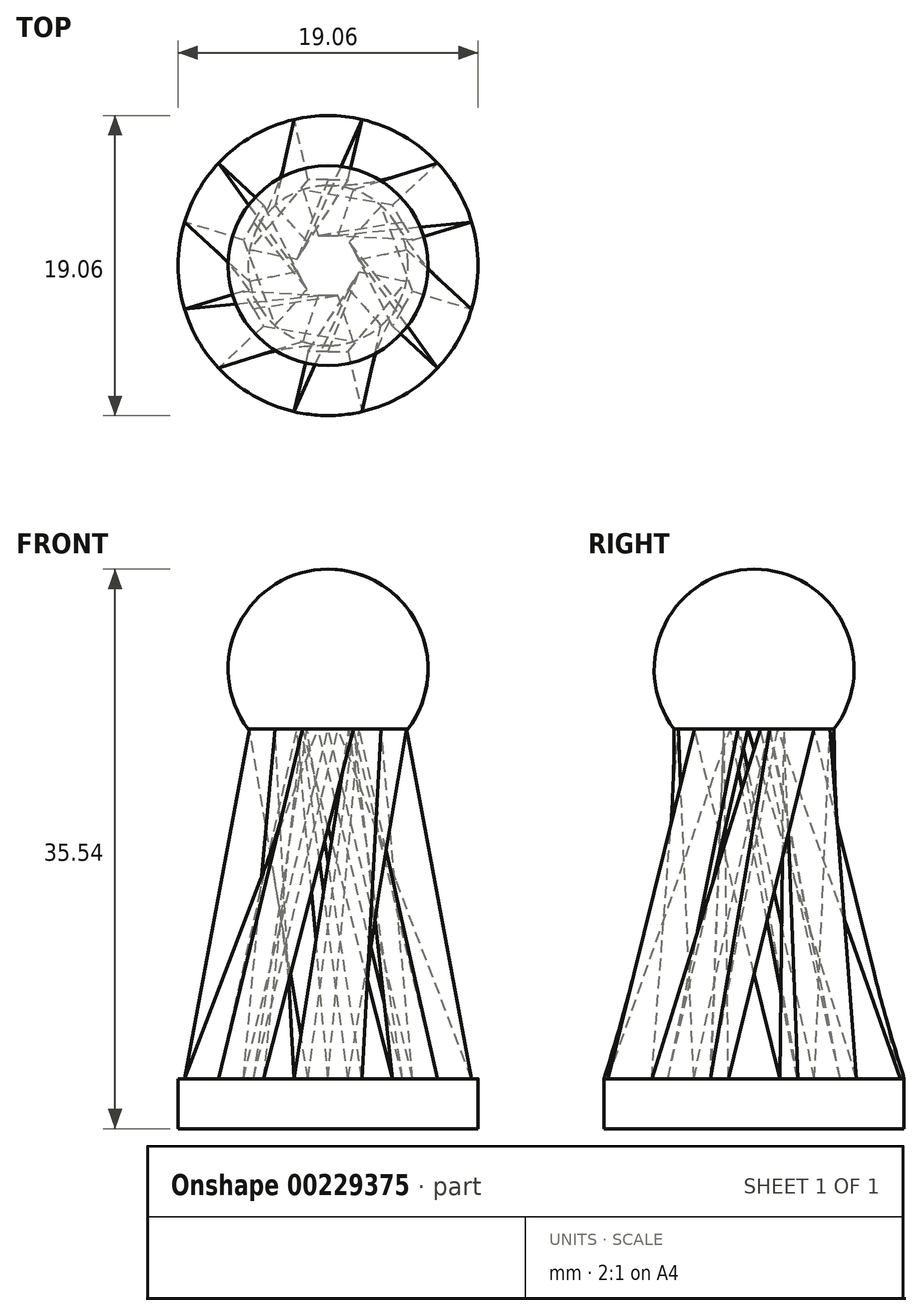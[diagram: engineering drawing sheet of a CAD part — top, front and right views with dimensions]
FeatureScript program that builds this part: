
annotation { "Feature Type Name" : "Feature", "Feature Type Description" : "" }
export const myFeature = defineFeature(function(context is Context, id is Id, definition is map)
    precondition{}
    {
        {
            var Q0;
            Q0=qCreatedBy(makeId("Top.planeOp"),FACE);
            var sketch = newSketch(context, id + "F0", { "sketchPlane" : qUnion([Q0])});
            skCircle(sketch, "E0", {"center": v(0, 0) * mm, "radius": 9.53 * mm});
            skSolve(sketch);
        }
        {
            var Q0;
            Q0=makeQuery(id+"F0.imprint","IMPRINT",FACE,{"disambiguationData":[TD([[makeQuery(id+"F0.imprint","IMPRINT",EDGE,{"derivedFrom":sQuery(id+"F0.wireOp",EDGE,"E0")}),1.0]])]});
            extrude(context, id + "F1", {"entities" : qUnion([Q0]), "depth" : 3.17 * mm});
        }
        {
            var Q0;
            Q0=makeQuery(id+"F1.opExtrude","CAP_FACE",FACE,{"disambiguationData":[OSD([sQuery(id+"F0.wireOp",EDGE,"E0")])],"isStart":false});
            var sketch = newSketch(context, id + "F2", { "sketchPlane" : qUnion([Q0])});
            skLineSegment(sketch, "E1", {"start": v(0, -5.47) * mm, "end": v(-1.27, -5.47) * mm});
            skLineSegment(sketch, "E2", {"start": v(0, -5.47) * mm, "end": v(1.27, -5.47) * mm});
            skLineSegment(sketch, "E3", {"start": v(-1.27, -5.47) * mm, "end": v(-2.15, -9.28) * mm});
            skLineSegment(sketch, "E4", {"start": v(1.27, -5.47) * mm, "end": v(2.15, -9.28) * mm});
            skLineSegment(sketch, "E5.1.0", {"start": v(-4.74, -2.73) * mm, "end": v(-5.37, -1.63) * mm});
            skLineSegment(sketch, "E5.1.1", {"start": v(-4.74, -2.73) * mm, "end": v(-4.1, -3.83) * mm});
            skLineSegment(sketch, "E5.1.2", {"start": v(-4.1, -3.83) * mm, "end": v(-6.96, -6.5) * mm});
            skLineSegment(sketch, "E5.1.3", {"start": v(-5.37, -1.63) * mm, "end": v(-9.11, -2.77) * mm});
            skLineSegment(sketch, "E5.2.0", {"start": v(-4.74, 2.73) * mm, "end": v(-4.1, 3.83) * mm});
            skLineSegment(sketch, "E5.2.1", {"start": v(-4.74, 2.73) * mm, "end": v(-5.37, 1.63) * mm});
            skLineSegment(sketch, "E5.2.2", {"start": v(-5.37, 1.63) * mm, "end": v(-9.11, 2.77) * mm});
            skLineSegment(sketch, "E5.2.3", {"start": v(-4.1, 3.83) * mm, "end": v(-6.96, 6.5) * mm});
            skLineSegment(sketch, "E5.3.0", {"start": v(0, 5.47) * mm, "end": v(1.27, 5.47) * mm});
            skLineSegment(sketch, "E5.3.1", {"start": v(0, 5.47) * mm, "end": v(-1.27, 5.47) * mm});
            skLineSegment(sketch, "E5.3.2", {"start": v(-1.27, 5.47) * mm, "end": v(-2.15, 9.28) * mm});
            skLineSegment(sketch, "E5.3.3", {"start": v(1.27, 5.47) * mm, "end": v(2.15, 9.28) * mm});
            skLineSegment(sketch, "E5.4.0", {"start": v(4.74, 2.73) * mm, "end": v(5.37, 1.63) * mm});
            skLineSegment(sketch, "E5.4.1", {"start": v(4.74, 2.73) * mm, "end": v(4.1, 3.83) * mm});
            skLineSegment(sketch, "E5.4.2", {"start": v(4.1, 3.83) * mm, "end": v(6.96, 6.5) * mm});
            skLineSegment(sketch, "E5.4.3", {"start": v(5.37, 1.63) * mm, "end": v(9.11, 2.77) * mm});
            skLineSegment(sketch, "E5.5.0", {"start": v(4.74, -2.73) * mm, "end": v(4.1, -3.83) * mm});
            skLineSegment(sketch, "E5.5.1", {"start": v(4.74, -2.73) * mm, "end": v(5.37, -1.63) * mm});
            skLineSegment(sketch, "E5.5.2", {"start": v(5.37, -1.63) * mm, "end": v(9.11, -2.77) * mm});
            skLineSegment(sketch, "E5.5.3", {"start": v(4.1, -3.83) * mm, "end": v(6.96, -6.5) * mm});
            skPoint(sketch, "E5.center", {"position": v(0, 0) * mm});
            skLineSegment(sketch, "E5.anchor1", {"start": v(0, 0) * mm, "end": v(-1.27, -5.47) * mm, "construction": true});
            skLineSegment(sketch, "E5.anchor2", {"start": v(0, 0) * mm, "end": v(4.1, -3.83) * mm, "construction": true});
            skArc(sketch, "E6", {"start": v(-2.15, -9.28) * mm, "mid": v(0, -9.52) * mm, "end": v(2.15, -9.28) * mm});
            skArc(sketch, "E7.trimOffspring", {"start": v(-9.11, -2.77) * mm, "mid": v(-8.25, -4.76) * mm, "end": v(-6.96, -6.5) * mm});
            skArc(sketch, "E8.trimOffspring", {"start": v(-6.96, 6.5) * mm, "mid": v(-8.25, 4.76) * mm, "end": v(-9.11, 2.77) * mm});
            skArc(sketch, "E9.trimOffspring", {"start": v(2.15, 9.28) * mm, "mid": v(0, 9.52) * mm, "end": v(-2.15, 9.28) * mm});
            skArc(sketch, "E10.trimOffspring", {"start": v(9.11, 2.77) * mm, "mid": v(8.25, 4.76) * mm, "end": v(6.96, 6.5) * mm});
            skArc(sketch, "E11.trimOffspring", {"start": v(6.96, -6.5) * mm, "mid": v(8.25, -4.76) * mm, "end": v(9.11, -2.77) * mm});
            skLineSegment(sketch, "E12", {"start": v(0, -5.47) * mm, "end": v(0, 0) * mm});
            skSolve(sketch);
        }
        {
            var Q0;
            Q0=qCreatedBy(makeId("Top.planeOp"),FACE);
            cPlane(context, id + "F3", {"entities" : qUnion([Q0]), "cplaneType" : CPlaneType.OFFSET, "offset" : 25.4 * mm, "width" : 152.4 * mm, "height" : 152.4 * mm});
        }
        {
            var Q0;
            Q0=qCreatedBy(id+"F3.planeOp",FACE);
            var sketch = newSketch(context, id + "F4", { "sketchPlane" : qUnion([Q0])});
            skArc(sketch, "E13", {"start": v(-1.6, -4.82) * mm, "mid": v(0, -5.08) * mm, "end": v(1.6, -4.82) * mm});
            skLineSegment(sketch, "E14", {"start": v(0, -1.9) * mm, "end": v(0.64, -1.9) * mm});
            skLineSegment(sketch, "E15", {"start": v(0, -1.9) * mm, "end": v(-0.64, -1.9) * mm});
            skLineSegment(sketch, "E16", {"start": v(-0.63, -1.9) * mm, "end": v(-1.6, -4.82) * mm});
            skLineSegment(sketch, "E17", {"start": v(0.63, -1.9) * mm, "end": v(1.6, -4.82) * mm});
            skLineSegment(sketch, "E18.1.0", {"start": v(1.33, -1.5) * mm, "end": v(3.37, -3.8) * mm});
            skLineSegment(sketch, "E18.1.1", {"start": v(1.65, -0.95) * mm, "end": v(1.33, -1.5) * mm});
            skLineSegment(sketch, "E18.1.2", {"start": v(1.65, -0.95) * mm, "end": v(1.97, -0.4) * mm});
            skLineSegment(sketch, "E18.1.3", {"start": v(1.97, -0.4) * mm, "end": v(4.98, -1.02) * mm});
            skLineSegment(sketch, "E18.2.0", {"start": v(1.97, 0.4) * mm, "end": v(4.98, 1.02) * mm});
            skLineSegment(sketch, "E18.2.1", {"start": v(1.65, 0.95) * mm, "end": v(1.97, 0.4) * mm});
            skLineSegment(sketch, "E18.2.2", {"start": v(1.65, 0.95) * mm, "end": v(1.33, 1.5) * mm});
            skLineSegment(sketch, "E18.2.3", {"start": v(1.33, 1.5) * mm, "end": v(3.37, 3.8) * mm});
            skLineSegment(sketch, "E18.3.0", {"start": v(0.63, 1.9) * mm, "end": v(1.6, 4.82) * mm});
            skLineSegment(sketch, "E18.3.1", {"start": v(0, 1.9) * mm, "end": v(0.64, 1.9) * mm});
            skLineSegment(sketch, "E18.3.2", {"start": v(0, 1.9) * mm, "end": v(-0.63, 1.9) * mm});
            skLineSegment(sketch, "E18.3.3", {"start": v(-0.63, 1.9) * mm, "end": v(-1.6, 4.82) * mm});
            skLineSegment(sketch, "E18.4.0", {"start": v(-1.33, 1.5) * mm, "end": v(-3.37, 3.8) * mm});
            skLineSegment(sketch, "E18.4.1", {"start": v(-1.65, 0.95) * mm, "end": v(-1.33, 1.5) * mm});
            skLineSegment(sketch, "E18.4.2", {"start": v(-1.65, 0.95) * mm, "end": v(-1.97, 0.4) * mm});
            skLineSegment(sketch, "E18.4.3", {"start": v(-1.97, 0.4) * mm, "end": v(-4.98, 1.02) * mm});
            skLineSegment(sketch, "E18.5.0", {"start": v(-1.97, -0.4) * mm, "end": v(-4.98, -1.02) * mm});
            skLineSegment(sketch, "E18.5.1", {"start": v(-1.65, -0.95) * mm, "end": v(-1.97, -0.4) * mm});
            skLineSegment(sketch, "E18.5.2", {"start": v(-1.65, -0.95) * mm, "end": v(-1.33, -1.5) * mm});
            skLineSegment(sketch, "E18.5.3", {"start": v(-1.33, -1.5) * mm, "end": v(-3.37, -3.8) * mm});
            skArc(sketch, "E19.trimOffspring", {"start": v(3.37, -3.8) * mm, "mid": v(4.4, -2.54) * mm, "end": v(4.98, -1.02) * mm});
            skArc(sketch, "E20.trimOffspring", {"start": v(4.98, 1.02) * mm, "mid": v(4.4, 2.54) * mm, "end": v(3.37, 3.8) * mm});
            skArc(sketch, "E21.trimOffspring", {"start": v(1.6, 4.82) * mm, "mid": v(0, 5.08) * mm, "end": v(-1.6, 4.82) * mm});
            skArc(sketch, "E22.trimOffspring", {"start": v(-3.37, 3.8) * mm, "mid": v(-4.4, 2.54) * mm, "end": v(-4.98, 1.02) * mm});
            skArc(sketch, "E23.trimOffspring", {"start": v(-4.98, -1.02) * mm, "mid": v(-4.4, -2.54) * mm, "end": v(-3.37, -3.8) * mm});
            skLineSegment(sketch, "E24", {"start": v(0, -1.9) * mm, "end": v(0, 0) * mm});
            skSolve(sketch);
        }
        {
            var Q1;
            Q1=makeQuery(id+"F2.imprint","IMPRINT",FACE,{"disambiguationData":[TD([[makeQuery(id+"F2.imprint","IMPRINT",EDGE,{"derivedFrom":sQuery(id+"F2.wireOp",EDGE,"E1")}),1.0]])]});
            var Q2;
            Q2=makeQuery(id+"F4.imprint","IMPRINT",FACE,{"disambiguationData":[TD([[makeQuery(id+"F4.imprint","IMPRINT",EDGE,{"derivedFrom":sQuery(id+"F4.wireOp",EDGE,"E18.1.0")}),1.0]])]});
            loft(context, id + "F5", {"operationType" : NewBodyOperationType.ADD, "sheetProfilesArray" : [{ "sheetProfileEntities" : qUnion([Q1]) }, { "sheetProfileEntities" : qUnion([Q2]) }]});
        }
        {
            var Q1;
            Q1=makeQuery(id+"F2.imprint","IMPRINT",FACE,{"disambiguationData":[TD([[makeQuery(id+"F2.imprint","IMPRINT",EDGE,{"derivedFrom":sQuery(id+"F2.wireOp",EDGE,"E5.1.0")}),1.0]])]});
            var Q2;
            Q2=makeQuery(id+"F4.imprint","IMPRINT",FACE,{"disambiguationData":[TD([[makeQuery(id+"F4.imprint","IMPRINT",EDGE,{"derivedFrom":sQuery(id+"F4.wireOp",EDGE,"E13")}),1.0]])]});
            loft(context, id + "F6", {"operationType" : NewBodyOperationType.ADD, "sheetProfilesArray" : [{ "sheetProfileEntities" : qUnion([Q1]) }, { "sheetProfileEntities" : qUnion([Q2]) }]});
        }
        {
            var Q1;
            Q1=makeQuery(id+"F2.imprint","IMPRINT",FACE,{"disambiguationData":[TD([[makeQuery(id+"F2.imprint","IMPRINT",EDGE,{"derivedFrom":sQuery(id+"F2.wireOp",EDGE,"E5.2.0")}),1.0]])]});
            var Q2;
            Q2=makeQuery(id+"F4.imprint","IMPRINT",FACE,{"disambiguationData":[TD([[makeQuery(id+"F4.imprint","IMPRINT",EDGE,{"derivedFrom":sQuery(id+"F4.wireOp",EDGE,"E18.5.0")}),1.0]])]});
            loft(context, id + "F7", {"operationType" : NewBodyOperationType.ADD, "sheetProfilesArray" : [{ "sheetProfileEntities" : qUnion([Q1]) }, { "sheetProfileEntities" : qUnion([Q2]) }]});
        }
        {
            var Q1;
            Q1=makeQuery(id+"F2.imprint","IMPRINT",FACE,{"disambiguationData":[TD([[makeQuery(id+"F2.imprint","IMPRINT",EDGE,{"derivedFrom":sQuery(id+"F2.wireOp",EDGE,"E5.5.0")}),1.0]])]});
            var Q2;
            Q2=makeQuery(id+"F4.imprint","IMPRINT",FACE,{"disambiguationData":[TD([[makeQuery(id+"F4.imprint","IMPRINT",EDGE,{"derivedFrom":sQuery(id+"F4.wireOp",EDGE,"E18.2.0")}),1.0]])]});
            loft(context, id + "F8", {"operationType" : NewBodyOperationType.ADD, "sheetProfilesArray" : [{ "sheetProfileEntities" : qUnion([Q1]) }, { "sheetProfileEntities" : qUnion([Q2]) }]});
        }
        {
            var Q1;
            Q1=makeQuery(id+"F2.imprint","IMPRINT",FACE,{"disambiguationData":[TD([[makeQuery(id+"F2.imprint","IMPRINT",EDGE,{"derivedFrom":sQuery(id+"F2.wireOp",EDGE,"E5.4.0")}),1.0]])]});
            var Q2;
            Q2=makeQuery(id+"F4.imprint","IMPRINT",FACE,{"disambiguationData":[TD([[makeQuery(id+"F4.imprint","IMPRINT",EDGE,{"derivedFrom":sQuery(id+"F4.wireOp",EDGE,"E18.3.0")}),1.0]])]});
            loft(context, id + "F9", {"operationType" : NewBodyOperationType.ADD, "sheetProfilesArray" : [{ "sheetProfileEntities" : qUnion([Q1]) }, { "sheetProfileEntities" : qUnion([Q2]) }]});
        }
        {
            var Q1;
            Q1=makeQuery(id+"F2.imprint","IMPRINT",FACE,{"disambiguationData":[TD([[makeQuery(id+"F2.imprint","IMPRINT",EDGE,{"derivedFrom":sQuery(id+"F2.wireOp",EDGE,"E5.3.0")}),1.0]])]});
            var Q2;
            Q2=makeQuery(id+"F4.imprint","IMPRINT",FACE,{"disambiguationData":[TD([[makeQuery(id+"F4.imprint","IMPRINT",EDGE,{"derivedFrom":sQuery(id+"F4.wireOp",EDGE,"E18.4.0")}),1.0]])]});
            loft(context, id + "F10", {"operationType" : NewBodyOperationType.ADD, "sheetProfilesArray" : [{ "sheetProfileEntities" : qUnion([Q1]) }, { "sheetProfileEntities" : qUnion([Q2]) }]});
        }
        {
            var Q0;
            Q0=qCreatedBy(makeId("Front.planeOp"),FACE);
            var sketch = newSketch(context, id + "F11", { "sketchPlane" : qUnion([Q0])});
            skLineSegment(sketch, "E25", {"start": v(0, 25.38) * mm, "end": v(0, 35.54) * mm});
            skLineSegment(sketch, "E26", {"start": v(0, 25.38) * mm, "end": v(5.08, 25.38) * mm});
            skArc(sketch, "E27", {"start": v(5.08, 25.38) * mm, "mid": v(5.68, 32.03) * mm, "end": v(0, 35.54) * mm});
            skSolve(sketch);
        }
        {
            var Q0;
            Q0=makeQuery(id+"F11.imprint","IMPRINT",FACE,{"disambiguationData":[TD([[makeQuery(id+"F11.imprint","IMPRINT",EDGE,{"derivedFrom":sQuery(id+"F11.wireOp",EDGE,"E25")}),-1.0]])]});
            var Q1;
            Q1=sQuery(id+"F11.wireOp",EDGE,"E25");
            revolve(context, id + "F12", {"operationType" : NewBodyOperationType.ADD, "entities" : qUnion([Q0]), "axis" : qUnion([Q1]), "revolveType" : RevolveType.FULL});
        }
        {
            var Q0;
            Q0=qCreatedBy(makeId("Right.planeOp"),FACE);
            var sketch = newSketch(context, id + "F13", { "sketchPlane" : qUnion([Q0])});
            skLineSegment(sketch, "E28", {"start": v(0, 25.4) * mm, "end": v(0, 3.18) * mm});
            skLineSegment(sketch, "E29", {"start": v(0, 25.4) * mm, "end": v(-1.9, 25.4) * mm});
            skLineSegment(sketch, "E30", {"start": v(0, 3.18) * mm, "end": v(-0.64, 3.18) * mm});
            skLineSegment(sketch, "E31", {"start": v(-0.63, 3.17) * mm, "end": v(-1.9, 25.4) * mm});
            skSolve(sketch);
        }
        {
            var Q0;
            Q0=qSketchRegion(id+"F13",true);
            var Q1;
            Q1=sQuery(id+"F13.wireOp",EDGE,"E28");
            revolve(context, id + "F14", {"entities" : qUnion([Q0]), "axis" : qUnion([Q1]), "revolveType" : RevolveType.FULL});
        }
        {
            var Q0;
            Q0=makeQuery(id+"F14.opRevolve","SWEPT_BODY",BODY,{"disambiguationData":[OSD([sQuery(id+"F13.wireOp",EDGE,"E28"),sQuery(id+"F13.wireOp",EDGE,"E29"),sQuery(id+"F13.wireOp",EDGE,"E30"),sQuery(id+"F13.wireOp",EDGE,"E31")])]});
            deleteBodies(context, id + "F15", {"entities" : qUnion([Q0])});
        }
    });
